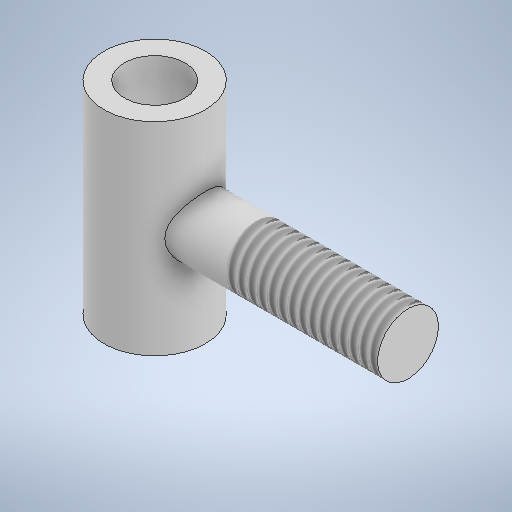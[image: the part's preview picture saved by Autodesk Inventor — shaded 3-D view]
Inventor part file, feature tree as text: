
AUTODESK INVENTOR PART (.ipt)
format: ipt  version: 2025.1 (Build 291241000, 241)  size: 284,160 bytes
history: native  units: mm
features: sketch x3, extrude x2, hole x1, plane x1, thread x1
ambient origin geometry x8: Origin, YZ Plane, XZ Plane, XY Plane, X Axis, Y Axis, Z Axis, Center Point
bodies: Solid1 (feature_tree)
feature tree (8):
  extrude  "Extrusion1"  Depth=10.0mm TaperAngle=0.0deg
  hole  "Hole1"  [1 undecoded]
  plane  "Work Plane1"
  extrude  "Extrusion2"  Depth=10.0mm TaperAngle=0.0deg
  thread  "Thread1"  [1 undecoded]
  sketch  "Sketch1"  dims[d0=10.0mm d1=20.0mm d2=0.0mm]
  sketch  "Sketch2"  dims[d3=6.0mm d4=6.0mm d5=4.0mm d6=2.0mm d7=90.0deg d8=8.0mm d9=0.0mm d10=25.0mm]
  sketch  "Sketch3"  dims[d11=6.0mm d12=10.0mm d13=0.0mm d14=15.0mm d15=0.0mm]
note: 2 required parameter values undecoded (feature->parameter linkage not recoverable at this tier; creation-order binding heuristic only, values carry confidence <= 0.55)
